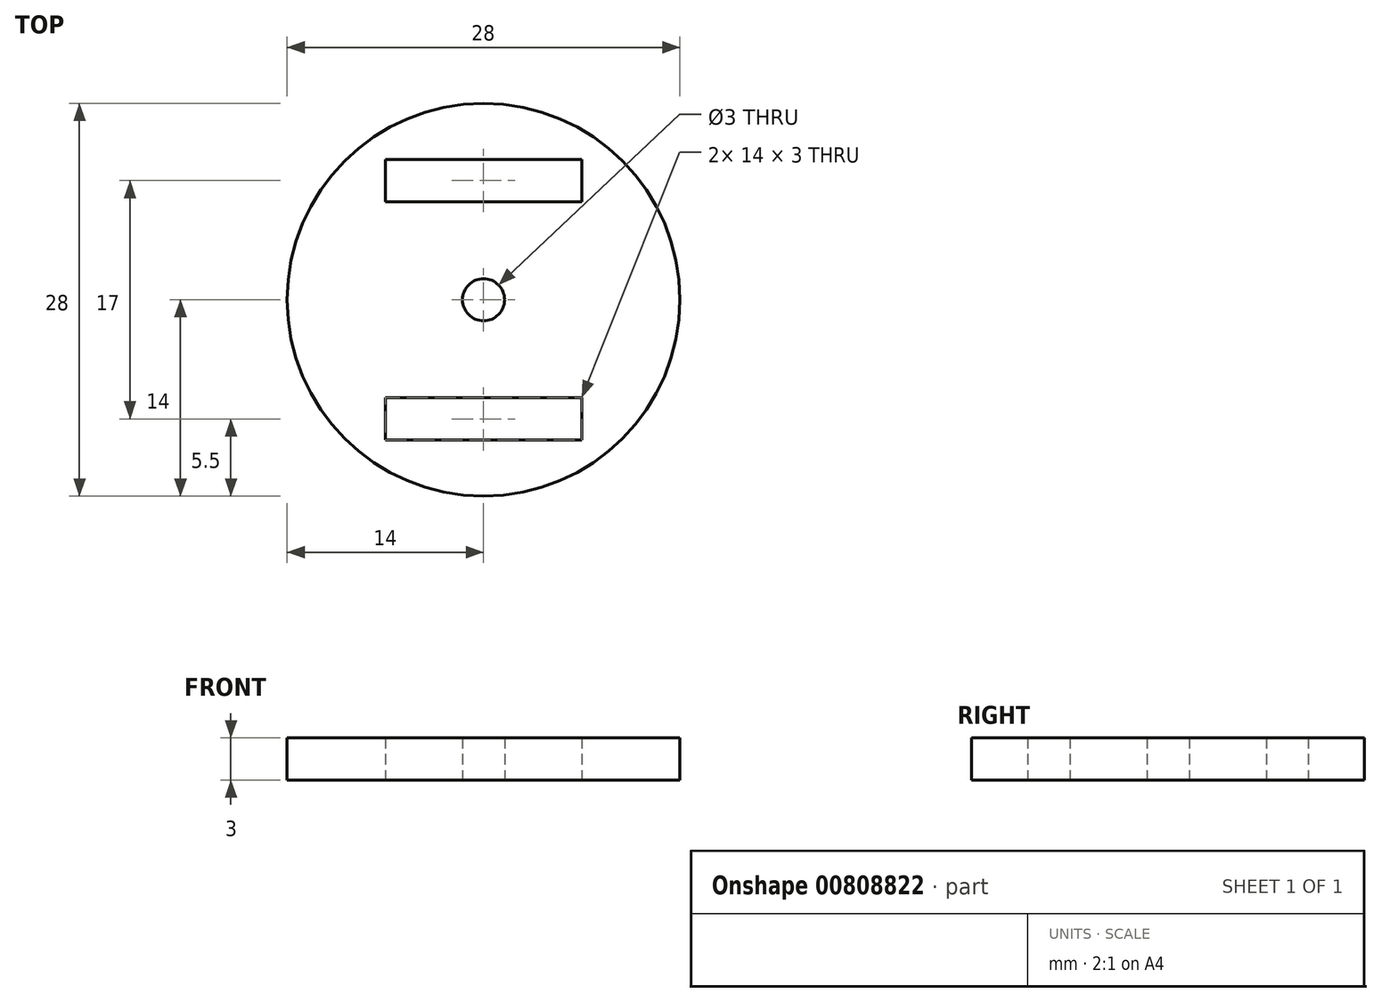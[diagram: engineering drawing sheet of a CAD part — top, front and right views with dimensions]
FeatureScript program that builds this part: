
annotation { "Feature Type Name" : "Feature", "Feature Type Description" : "" }
export const myFeature = defineFeature(function(context is Context, id is Id, definition is map)
    precondition{}
    {
        {
            var Q0;
            Q0=qCreatedBy(makeId("Top.planeOp"),FACE);
            var sketch = newSketch(context, id + "F0", { "sketchPlane" : qUnion([Q0])});
            skCircle(sketch, "E0", {"center": v(0, 0) * mm, "radius": 14 * mm});
            skCircle(sketch, "E1", {"center": v(0, 0) * mm, "radius": 1.5 * mm});
            skLineSegment(sketch, "E2.bottom", {"start": v(7, 7) * mm, "end": v(-7, 7) * mm});
            skLineSegment(sketch, "E2.top", {"start": v(7, 10) * mm, "end": v(-7, 10) * mm});
            skLineSegment(sketch, "E2.left", {"start": v(7, 7) * mm, "end": v(7, 10) * mm});
            skLineSegment(sketch, "E2.right", {"start": v(-7, 7) * mm, "end": v(-7, 10) * mm});
            skPoint(sketch, "E2.middle", {"position": v(0, 8.5) * mm});
            skLineSegment(sketch, "E3.bottom", {"start": v(7, -7) * mm, "end": v(-7, -7) * mm});
            skLineSegment(sketch, "E3.top", {"start": v(7, -10) * mm, "end": v(-7, -10) * mm});
            skLineSegment(sketch, "E3.left", {"start": v(7, -7) * mm, "end": v(7, -10) * mm});
            skLineSegment(sketch, "E3.right", {"start": v(-7, -7) * mm, "end": v(-7, -10) * mm});
            skPoint(sketch, "E3.middle", {"position": v(0, -8.5) * mm});
            skSolve(sketch);
        }
        {
            var Q0;
            Q0=qSketchRegion(id+"F0",true);
            extrude(context, id + "F1", {"entities" : qUnion([Q0]), "depth" : 3 * mm, "offsetDistance" : 25 * mm});
        }
    });
